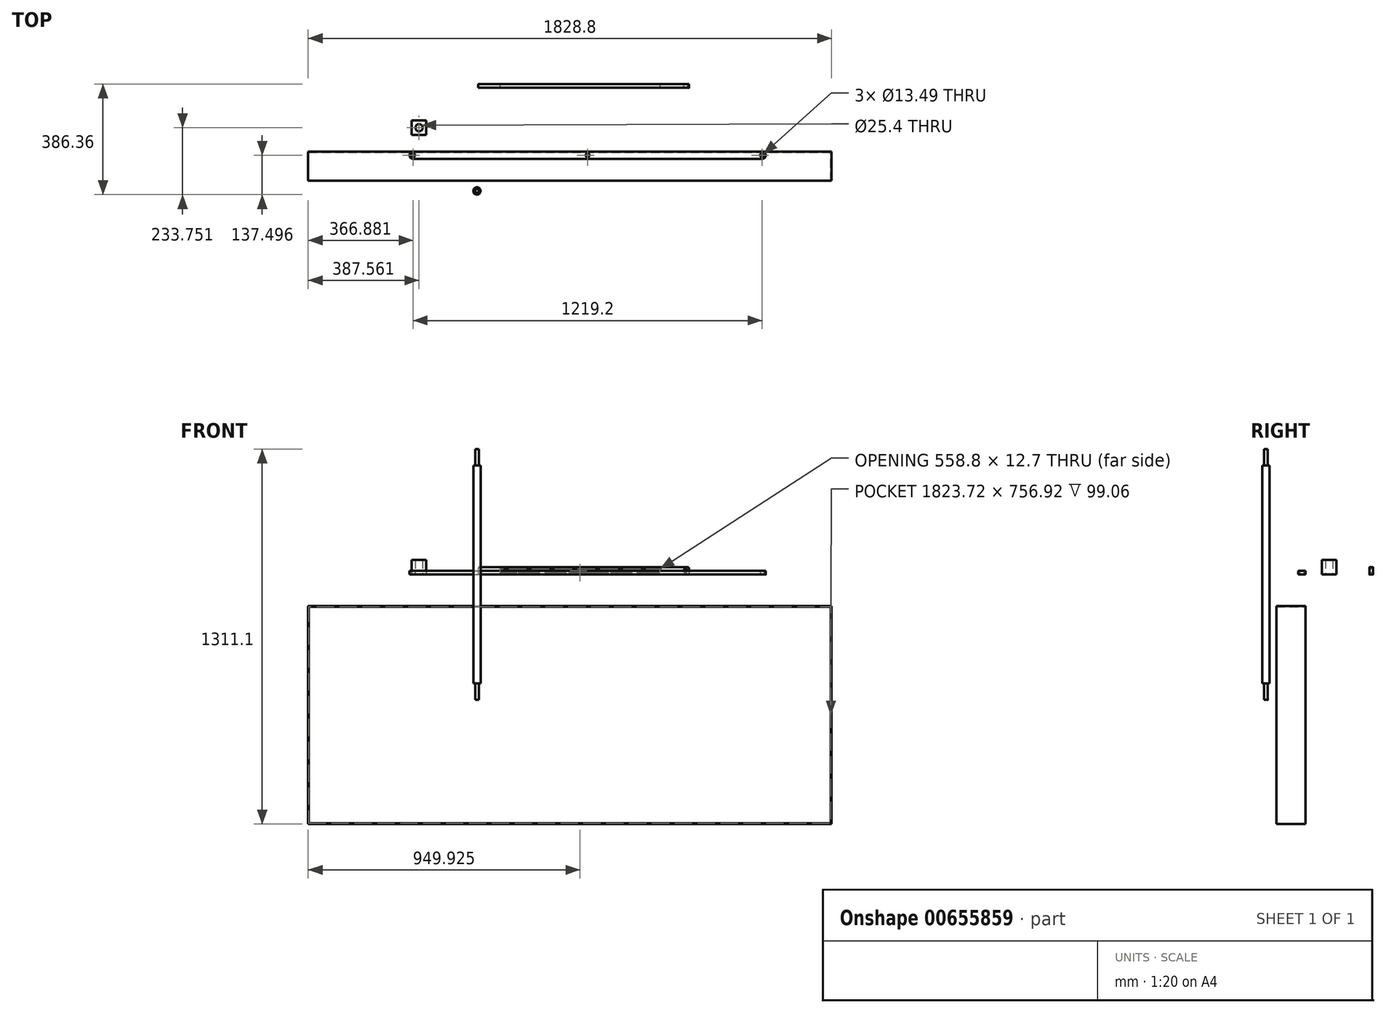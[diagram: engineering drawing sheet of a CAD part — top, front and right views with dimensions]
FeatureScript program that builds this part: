
annotation { "Feature Type Name" : "Feature", "Feature Type Description" : "" }
export const myFeature = defineFeature(function(context is Context, id is Id, definition is map)
    precondition{}
    {
        {
            var Q0;
            Q0=qCreatedBy(makeId("Front.planeOp"),FACE);
            var sketch = newSketch(context, id + "F0", { "sketchPlane" : qUnion([Q0])});
            skLineSegment(sketch, "E0.bottom", {"start": v(-141.46, 0) * mm, "end": v(1103.14, 0) * mm});
            skLineSegment(sketch, "E0.top", {"start": v(-141.46, 12.7) * mm, "end": v(1103.14, 12.7) * mm});
            skLineSegment(sketch, "E0.left", {"start": v(-141.46, 0) * mm, "end": v(-141.46, 12.7) * mm});
            skLineSegment(sketch, "E0.right", {"start": v(1103.14, 0) * mm, "end": v(1103.14, 12.7) * mm});
            skSolve(sketch);
        }
        {
            var Q0;
            Q0 = qSketchRegion(id + "F0", true);
            extrude(context, id + "F1", {"entities" : qUnion([Q0]), "depth" : 25.4 * mm, "offsetDistance" : 25.4 * mm});
        }
        {
            var Q0;
            Q0=makeQuery(id+"F1.opExtrude","CAP_EDGE",EDGE,{"disambiguationData":[OSD([sQuery(id+"F0.wireOp",EDGE,"E0.left")])],"isStart":false});
            var Q1;
            Q1=makeQuery(id+"F1.opExtrude","CAP_EDGE",EDGE,{"disambiguationData":[OSD([sQuery(id+"F0.wireOp",EDGE,"E0.right")])],"isStart":false});
            var Q2;
            Q2=makeQuery(id+"F1.opExtrude","CAP_EDGE",EDGE,{"disambiguationData":[OSD([sQuery(id+"F0.wireOp",EDGE,"E0.right")])],"isStart":true});
            var Q3;
            Q3=makeQuery(id+"F1.opExtrude","CAP_EDGE",EDGE,{"disambiguationData":[OSD([sQuery(id+"F0.wireOp",EDGE,"E0.left")])],"isStart":true});
            fillet(context, id + "F2", {"entities" : qUnion([Q0, Q1, Q2, Q3]), "radius" : 12.7 * mm, "tangentPropagation" : true, "allowEdgeOverflow" : false});
        }
        {
            var Q0;
            Q0=qCreatedBy(makeId("Top.planeOp"),FACE);
            var sketch = newSketch(context, id + "F3", { "sketchPlane" : qUnion([Q0])});
            skCircle(sketch, "E1", {"center": v(-128.76, -12.7) * mm, "radius": 6.35 * mm});
            skCircle(sketch, "E2", {"center": v(1090.44, -12.7) * mm, "radius": 6.35 * mm});
            skCircle(sketch, "E3", {"center": v(480.84, -12.7) * mm, "radius": 6.35 * mm});
            skSolve(sketch);
        }
        {
            var Q0;
            Q0=sQuery(id+"F3.wireOp",VERTEX,"E3.center");
            var Q1;
            Q1=sQuery(id+"F3.wireOp",VERTEX,"E2.center");
            var Q2;
            Q2=sQuery(id+"F3.wireOp",VERTEX,"E1.center");
            var Q3;
            Q3=makeQuery(id+"F1.opExtrude","SWEPT_BODY",BODY,{"disambiguationData":[OSD([sQuery(id+"F0.wireOp",EDGE,"E0.bottom"),sQuery(id+"F0.wireOp",EDGE,"E0.top"),sQuery(id+"F0.wireOp",EDGE,"E0.left"),sQuery(id+"F0.wireOp",EDGE,"E0.right")])]});
            hole(context, id + "F4", {"style" : HoleStyle.SIMPLE, "endStyle" : HoleEndStyle.THROUGH, "oppositeDirection" : true, "standardTappedOrClearance" : lookupTablePath({ "standard" : "ANSI", "fit" : "Normal (ASME)", "size" : "1/2", "type" : "Clearance" }), "standardBlindInLast" : lookupTablePath({ "fit" : "Free", "standard" : "ANSI", "size" : "1/2", "type" : "Clearance" }), "holeDiameter" : 13.5 * mm, "majorDiameter" : 6.35 * mm, "isTappedThrough" : true, "tappedDepth" : 12.7 * mm, "tapClearance" : 3, "startFromSketch" : true, "locations" : qUnion([Q0, Q1, Q2]), "scope" : qUnion([Q3])});
        }
        {
            var Q0;
            Q0=qCreatedBy(makeId("Top.planeOp"),FACE);
            var sketch = newSketch(context, id + "F5", { "sketchPlane" : qUnion([Q0])});
            skCircle(sketch, "E4", {"center": v(94.25, -137.5) * mm, "radius": 12.7 * mm});
            skCircle(sketch, "E5", {"center": v(94.25, -137.5) * mm, "radius": 6.35 * mm});
            skSolve(sketch);
        }
        {
            var Q0;
            Q0=makeQuery(id+"F5.imprint","IMPRINT",FACE,{"disambiguationData":[TD([[makeQuery(id+"F5.imprint","IMPRINT",EDGE,{"derivedFrom":sQuery(id+"F5.wireOp",EDGE,"E5")}),1.0]])]});
            extrude(context, id + "F6", {"entities" : qUnion([Q0]), "endBound" : BoundingType.SYMMETRIC, "depth" : 876.3 * mm, "offsetDistance" : 25.4 * mm});
        }
        {
            var Q0;
            Q0 = qSketchRegion(id + "F5", true);
            extrude(context, id + "F7", {"entities" : qUnion([Q0]), "operationType" : NewBodyOperationType.ADD, "endBound" : BoundingType.SYMMETRIC, "depth" : 762 * mm, "offsetDistance" : 25.4 * mm});
        }
        {
            var Q0;
            Q0=qCreatedBy(makeId("Top.planeOp"),FACE);
            var sketch = newSketch(context, id + "F8", { "sketchPlane" : qUnion([Q0])});
            skLineSegment(sketch, "E6.bottom", {"start": v(-133.48, 108.95) * mm, "end": v(-82.68, 108.95) * mm});
            skLineSegment(sketch, "E6.top", {"start": v(-133.48, 58.15) * mm, "end": v(-82.68, 58.15) * mm});
            skLineSegment(sketch, "E6.left", {"start": v(-133.48, 108.95) * mm, "end": v(-133.48, 58.15) * mm});
            skLineSegment(sketch, "E6.right", {"start": v(-82.68, 108.95) * mm, "end": v(-82.68, 58.15) * mm});
            skSolve(sketch);
        }
        {
            var Q0;
            Q0 = qSketchRegion(id + "F8", true);
            extrude(context, id + "F9", {"entities" : qUnion([Q0]), "depth" : 50.8 * mm, "offsetDistance" : 25.4 * mm});
        }
        {
            var Q0;
            Q0=qCreatedBy(makeId("Top.planeOp"),FACE);
            var sketch = newSketch(context, id + "F10", { "sketchPlane" : qUnion([Q0])});
            skCircle(sketch, "E7", {"center": v(-108.08, 83.55) * mm, "radius": 12.7 * mm});
            skSolve(sketch);
        }
        {
            var Q0;
            Q0=sQuery(id+"F10.wireOp",VERTEX,"E7.center");
            var Q1;
            Q1=makeQuery(id+"F9.opExtrude","SWEPT_BODY",BODY,{"disambiguationData":[OSD([sQuery(id+"F8.wireOp",EDGE,"E6.bottom"),sQuery(id+"F8.wireOp",EDGE,"E6.top"),sQuery(id+"F8.wireOp",EDGE,"E6.left"),sQuery(id+"F8.wireOp",EDGE,"E6.right")])]});
            hole(context, id + "F11", {"style" : HoleStyle.SIMPLE, "endStyle" : HoleEndStyle.THROUGH, "oppositeDirection" : true, "holeDiameter" : 25.4 * mm, "majorDiameter" : 6.35 * mm, "isTappedThrough" : true, "tappedDepth" : 12.7 * mm, "tapClearance" : 3, "startFromSketch" : true, "locations" : qUnion([Q0]), "scope" : qUnion([Q1])});
        }
        {
            var Q0;
            Q0=qCreatedBy(makeId("Top.planeOp"),FACE);
            var sketch = newSketch(context, id + "F12", { "sketchPlane" : qUnion([Q0])});
            skLineSegment(sketch, "E8.bottom", {"start": v(98.69, 223.46) * mm, "end": v(835.29, 223.46) * mm});
            skLineSegment(sketch, "E8.top", {"start": v(98.69, 236.16) * mm, "end": v(835.29, 236.16) * mm});
            skLineSegment(sketch, "E8.left", {"start": v(98.69, 223.46) * mm, "end": v(98.69, 236.16) * mm});
            skLineSegment(sketch, "E8.right", {"start": v(835.29, 223.46) * mm, "end": v(835.29, 236.16) * mm});
            skSolve(sketch);
        }
        {
            var Q0;
            Q0 = qSketchRegion(id + "F12", true);
            extrude(context, id + "F13", {"entities" : qUnion([Q0]), "depth" : 25.4 * mm, "offsetDistance" : 25.4 * mm});
        }
        {
            var Q0;
            Q0=qCreatedBy(makeId("Front.planeOp"),FACE);
            var sketch = newSketch(context, id + "F14", { "sketchPlane" : qUnion([Q0])});
            skLineSegment(sketch, "E9.bottom", {"start": v(174.89, 19.05) * mm, "end": v(733.69, 19.05) * mm});
            skLineSegment(sketch, "E9.top", {"start": v(174.89, 6.35) * mm, "end": v(733.69, 6.35) * mm});
            skLineSegment(sketch, "E9.left", {"start": v(174.89, 19.05) * mm, "end": v(174.89, 6.35) * mm});
            skLineSegment(sketch, "E9.right", {"start": v(733.69, 19.05) * mm, "end": v(733.69, 6.35) * mm});
            skCircle(sketch, "E10", {"center": v(822.59, 12.7) * mm, "radius": 6.35 * mm});
            skSolve(sketch);
        }
        {
            var Q0;
            Q0 = qSketchRegion(id + "F14", true);
            extrude(context, id + "F15", {"entities" : qUnion([Q0]), "endBound" : BoundingType.THROUGH_ALL, "oppositeDirection" : true, "depth" : 152.4 * mm, "offsetDistance" : 25.4 * mm});
        }
        {
            var Q0;
            Q0=makeQuery(id+"F15.opExtrude","SWEPT_BODY",BODY,{"disambiguationData":[OSD([sQuery(id+"F14.wireOp",EDGE,"E9.bottom"),sQuery(id+"F14.wireOp",EDGE,"E9.top"),sQuery(id+"F14.wireOp",EDGE,"E9.left"),sQuery(id+"F14.wireOp",EDGE,"E9.right")])]});
            var Q1;
            Q1=makeQuery(id+"F15.opExtrude","SWEPT_BODY",BODY,{"disambiguationData":[OSD([sQuery(id+"F14.wireOp",EDGE,"E10")])]});
            var Q2;
            Q2=makeQuery(id+"F13.opExtrude","SWEPT_BODY",BODY,{"disambiguationData":[OSD([sQuery(id+"F12.wireOp",EDGE,"E8.bottom"),sQuery(id+"F12.wireOp",EDGE,"E8.top"),sQuery(id+"F12.wireOp",EDGE,"E8.left"),sQuery(id+"F12.wireOp",EDGE,"E8.right")])]});
            booleanBodies(context, id + "F16", {"operationType" : BooleanOperationType.SUBTRACTION, "tools" : qUnion([Q0, Q1]), "targets" : qUnion([Q2])});
        }
        {
            var Q0;
            Q0=makeQuery(id+"F13.opExtrude","CAP_EDGE",EDGE,{"disambiguationData":[OSD([sQuery(id+"F12.wireOp",EDGE,"E8.left")])],"isStart":false});
            var Q1;
            Q1=makeQuery(id+"F13.opExtrude","CAP_EDGE",EDGE,{"disambiguationData":[OSD([sQuery(id+"F12.wireOp",EDGE,"E8.right")])],"isStart":false});
            var Q2;
            Q2=makeQuery(id+"F16.opBoolean","COPY",EDGE,{"derivedFrom":makeQuery(id+"F15.opExtrude","SWEPT_EDGE",EDGE,{"disambiguationData":[OSD([sQuery(id+"F14.wireOp",EDGE,"E9.top"),sQuery(id+"F14.wireOp",EDGE,"E9.right")])]})});
            var Q3;
            Q3=makeQuery(id+"F16.opBoolean","COPY",EDGE,{"derivedFrom":makeQuery(id+"F15.opExtrude","SWEPT_EDGE",EDGE,{"disambiguationData":[OSD([sQuery(id+"F14.wireOp",EDGE,"E9.top"),sQuery(id+"F14.wireOp",EDGE,"E9.left")])]})});
            var Q4;
            Q4=makeQuery(id+"F16.opBoolean","COPY",EDGE,{"derivedFrom":makeQuery(id+"F15.opExtrude","SWEPT_EDGE",EDGE,{"disambiguationData":[OSD([sQuery(id+"F14.wireOp",EDGE,"E9.bottom"),sQuery(id+"F14.wireOp",EDGE,"E9.left")])]})});
            var Q5;
            Q5=makeQuery(id+"F13.opExtrude","CAP_EDGE",EDGE,{"disambiguationData":[OSD([sQuery(id+"F12.wireOp",EDGE,"E8.left")])],"isStart":true});
            var Q6;
            Q6=makeQuery(id+"F13.opExtrude","CAP_EDGE",EDGE,{"disambiguationData":[OSD([sQuery(id+"F12.wireOp",EDGE,"E8.right")])],"isStart":true});
            var Q7;
            Q7=makeQuery(id+"F16.opBoolean","COPY",EDGE,{"derivedFrom":makeQuery(id+"F15.opExtrude","SWEPT_EDGE",EDGE,{"disambiguationData":[OSD([sQuery(id+"F14.wireOp",EDGE,"E9.bottom"),sQuery(id+"F14.wireOp",EDGE,"E9.right")])]})});
            fillet(context, id + "F17", {"entities" : qUnion([Q0, Q1, Q2, Q3, Q4, Q5, Q6, Q7]), "radius" : 5.08 * mm, "tangentPropagation" : true, "allowEdgeOverflow" : false});
        }
        {
            var Q0;
            Q0=qCreatedBy(makeId("Front.planeOp"),FACE);
            var sketch = newSketch(context, id + "F18", { "sketchPlane" : qUnion([Q0])});
            skLineSegment(sketch, "E11.bottom", {"start": v(-495.64, -110.95) * mm, "end": v(1333.16, -110.95) * mm});
            skLineSegment(sketch, "E11.top", {"start": v(-495.64, -872.95) * mm, "end": v(1333.16, -872.95) * mm});
            skLineSegment(sketch, "E11.left", {"start": v(-495.64, -110.95) * mm, "end": v(-495.64, -872.95) * mm});
            skLineSegment(sketch, "E11.right", {"start": v(1333.16, -110.95) * mm, "end": v(1333.16, -872.95) * mm});
            skSolve(sketch);
        }
        {
            var Q0;
            Q0 = qSketchRegion(id + "F18", true);
            extrude(context, id + "F19", {"entities" : qUnion([Q0]), "depth" : 101.6 * mm, "offsetDistance" : 25.4 * mm});
        }
        {
            var Q0;
            Q0=makeQuery(id+"F19.opExtrude","CAP_FACE",FACE,{"disambiguationData":[OSD([sQuery(id+"F18.wireOp",EDGE,"E11.bottom"),sQuery(id+"F18.wireOp",EDGE,"E11.top"),sQuery(id+"F18.wireOp",EDGE,"E11.left"),sQuery(id+"F18.wireOp",EDGE,"E11.right")])],"isStart":false});
            shell(context, id + "F20", {"entities" : qUnion([Q0]), "thickness" : 2.54 * mm});
        }
    });
